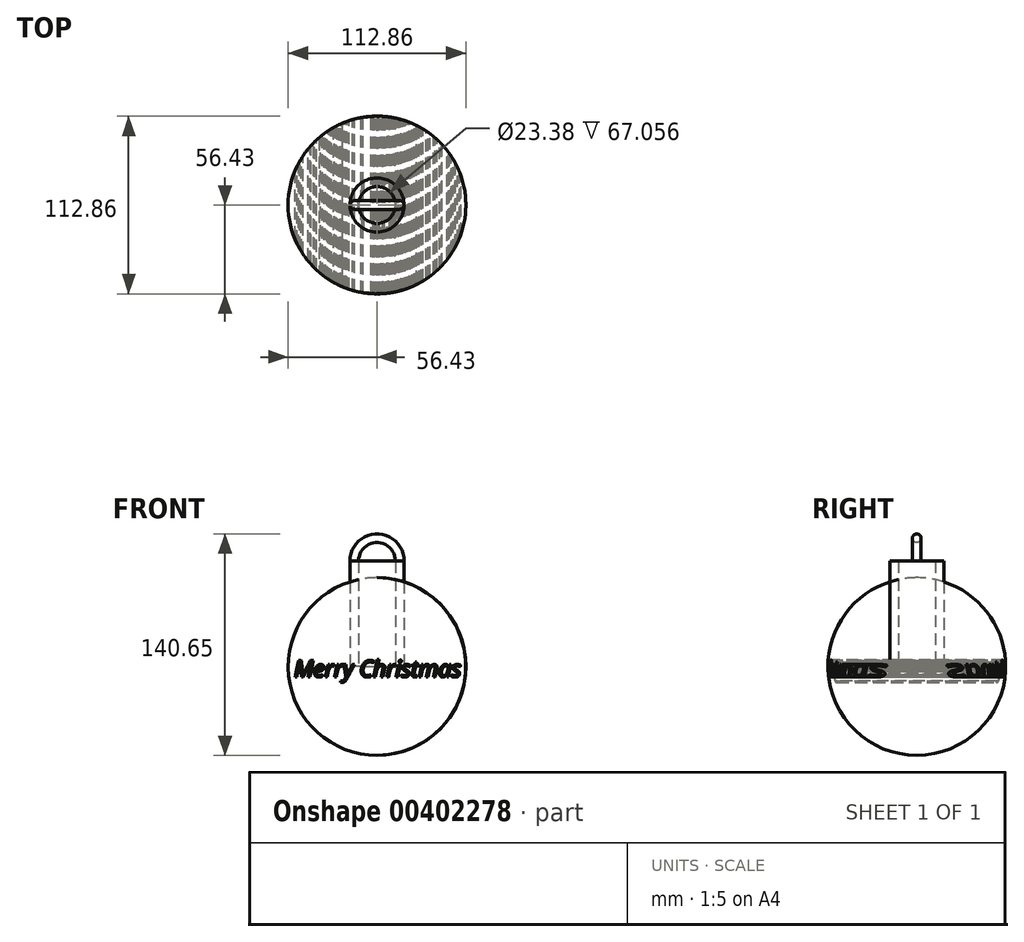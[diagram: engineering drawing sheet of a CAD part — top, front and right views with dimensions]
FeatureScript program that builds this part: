
annotation { "Feature Type Name" : "Feature", "Feature Type Description" : "" }
export const myFeature = defineFeature(function(context is Context, id is Id, definition is map)
    precondition{}
    {
        {
            var Q0;
            Q0=qCreatedBy(makeId("Front.planeOp"),FACE);
            var sketch = newSketch(context, id + "F0", { "sketchPlane" : qUnion([Q0])});
            skLineSegment(sketch, "E0", {"start": v(0, 75.8) * mm, "end": v(0, -77.23) * mm});
            skCircle(sketch, "E1", {"center": v(0, 0) * mm, "radius": 56.43 * mm});
            skSolve(sketch);
        }
        {
            var Q0;
            {var subQ0=sQuery(id+"F0.wireOp",EDGE,"E1");var subQ1=sQuery(id+"F0.wireOp",EDGE,"E0");var subQ2=makeQuery(id+"F0.imprint","INTERSECT",VERTEX,{"disambiguationData":[OD(0.0)],"derivedFrom":[subQ1,subQ0]});Q0=makeQuery(id+"F0.imprint","IMPRINT",FACE,{"disambiguationData":[TD([[makeQuery(id+"F0.imprint","IMPRINT",EDGE,{"disambiguationData":[TD([[subQ2,1.0]])],"derivedFrom":subQ1}),1.0]])]});}
            var Q1;
            Q1=sQuery(id+"F0.wireOp",EDGE,"E0");
            revolve(context, id + "F1", {"entities" : qUnion([Q0]), "axis" : qUnion([Q1]), "revolveType" : RevolveType.FULL});
        }
        {
            var Q0;
            Q0=qCreatedBy(makeId("Top.planeOp"),FACE);
            var sketch = newSketch(context, id + "F2", { "sketchPlane" : qUnion([Q0])});
            skCircle(sketch, "E2", {"center": v(0, 0) * mm, "radius": 11.7 * mm});
            skCircle(sketch, "E3", {"center": v(0, 0) * mm, "radius": 17.17 * mm});
            skSolve(sketch);
        }
        {
            var Q0;
            Q0 = qSketchRegion(id + "F2", true);
            extrude(context, id + "F3", {"entities" : qUnion([Q0]), "depth" : 67.06 * mm});
        }
        {
            var Q0;
            Q0=makeQuery(id+"F3.opExtrude","CAP_FACE",FACE,{"disambiguationData":[OSD([sQuery(id+"F2.wireOp",EDGE,"E2"),sQuery(id+"F2.wireOp",EDGE,"E3")])],"isStart":false});
            var sketch = newSketch(context, id + "F4", { "sketchPlane" : qUnion([Q0])});
            skCircle(sketch, "E4", {"center": v(14.43, 0) * mm, "radius": 2.74 * mm});
            skCircle(sketch, "E5", {"center": v(-14.43, 0) * mm, "radius": 2.74 * mm});
            skSolve(sketch);
        }
        {
            var Q0;
            Q0=qCreatedBy(makeId("Front.planeOp"),FACE);
            var sketch = newSketch(context, id + "F5", { "sketchPlane" : qUnion([Q0])});
            skArc(sketch, "E6", {"start": v(14.43, 67.06) * mm, "mid": v(0, 81.49) * mm, "end": v(-14.43, 67.06) * mm});
            skSolve(sketch);
        }
        {
            var Q0;
            {var subQ0=sQuery(id+"F4.wireOp",EDGE,"E4");var subQ1=makeQuery(id+"F4.imprint","INTERSECT",VERTEX,{"derivedFrom":[makeQuery(id+"F3.opExtrude","CAP_EDGE",EDGE,{"disambiguationData":[OSD([sQuery(id+"F2.wireOp",EDGE,"E3")])],"isStart":false}),subQ0]});Q0=makeQuery(id+"F4.imprint","IMPRINT",FACE,{"disambiguationData":[TD([[makeQuery(id+"F4.imprint","IMPRINT",EDGE,{"disambiguationData":[TD([[subQ1,-1.0]])],"derivedFrom":subQ0}),1.0]])]});}
            var Q1;
            Q1=sQuery(id+"F5.wireOp",EDGE,"E6");
            sweep(context, id + "F6", {"profiles" : qUnion([Q0]), "path" : qUnion([Q1])});
        }
        {
            var Q0;
            Q0=qCreatedBy(makeId("Front.planeOp"),FACE);
            var sketch = newSketch(context, id + "F7", { "sketchPlane" : qUnion([Q0])});
            skText(sketch, "E7", { "text": "Merry Christmas", "fontName": "OpenSans-Italic.ttf"});
            const initialGuessF7  = {"E7": [-0.05267, -0.00662, 1, 0, 0.01051]};
            skSetInitialGuess(sketch, initialGuessF7);
            skSolve(sketch);
        }
        {
            var Q0;
            Q0 = qSketchRegion(id + "F7", true);
            extrude(context, id + "F8", {"entities" : qUnion([Q0]), "operationType" : NewBodyOperationType.REMOVE, "endBound" : BoundingType.SYMMETRIC, "depth" : 274.83 * mm});
        }
    });
